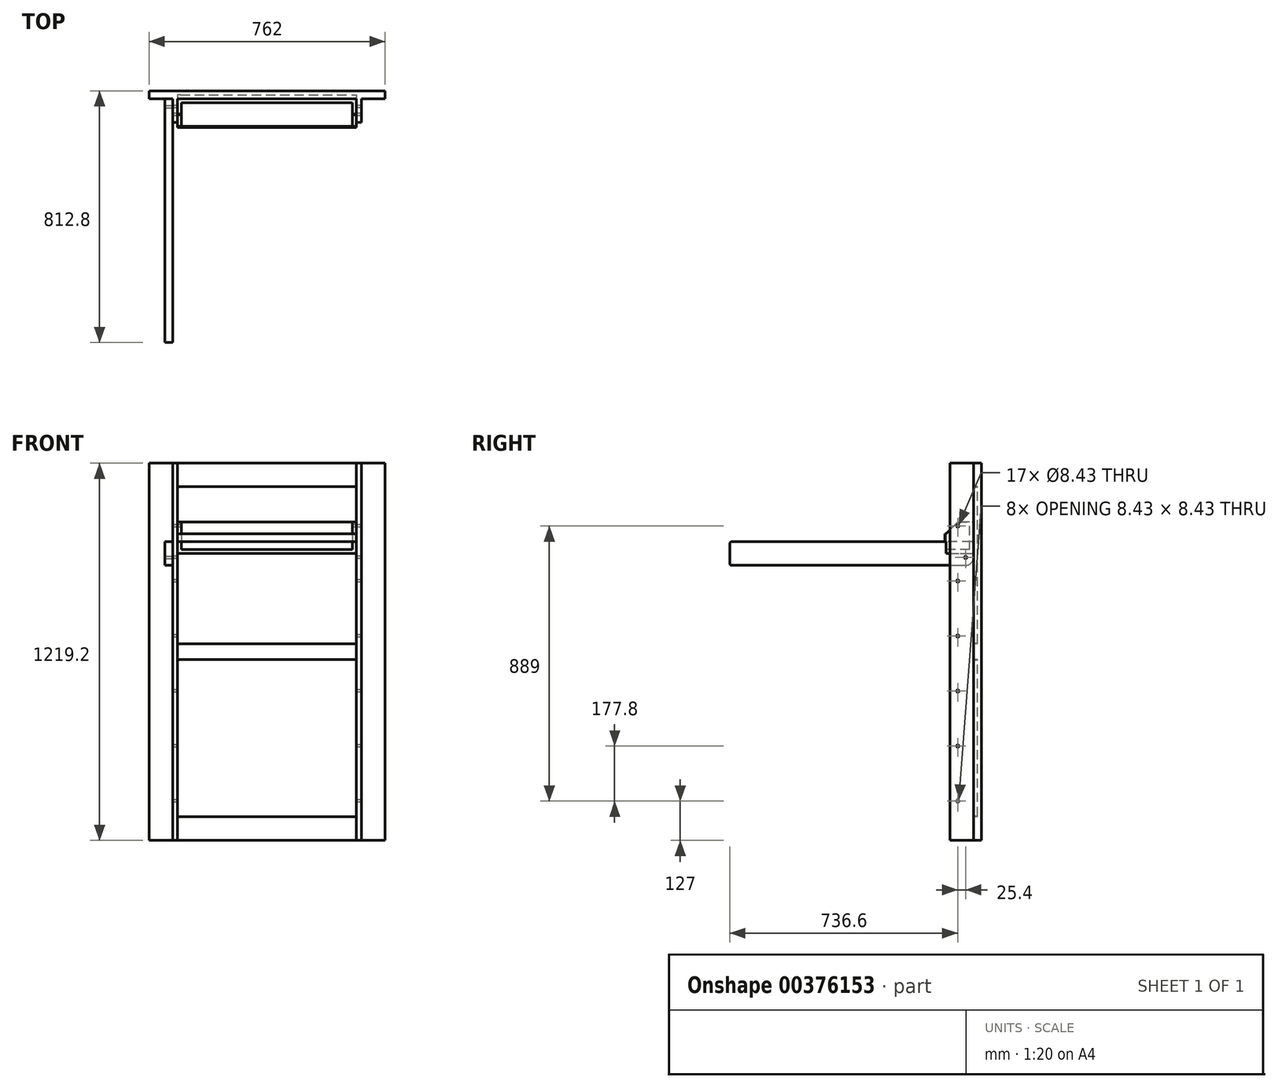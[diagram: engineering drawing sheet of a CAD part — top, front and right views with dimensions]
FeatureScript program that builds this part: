
annotation { "Feature Type Name" : "Feature", "Feature Type Description" : "" }
export const myFeature = defineFeature(function(context is Context, id is Id, definition is map)
    precondition{}
    {
        {
            var Q0;
            Q0=qCreatedBy(makeId("Front.planeOp"),FACE);
            var sketch = newSketch(context, id + "F0", { "sketchPlane" : qUnion([Q0])});
            skLineSegment(sketch, "E0.bottom", {"start": v(-381, 1219.2) * mm, "end": v(381, 1219.2) * mm});
            skLineSegment(sketch, "E0.top", {"start": v(-381, 0) * mm, "end": v(381, 0) * mm});
            skLineSegment(sketch, "E0.left", {"start": v(-381, 1219.2) * mm, "end": v(-381, 0) * mm});
            skLineSegment(sketch, "E0.right", {"start": v(381, 1219.2) * mm, "end": v(381, 0) * mm});
            skSolve(sketch);
        }
        {
            var Q0;
            Q0 = qSketchRegion(id + "F0", true);
            extrude(context, id + "F1", {"entities" : qUnion([Q0]), "depth" : 25.4 * mm});
        }
        {
            var Q0;
            Q0=makeQuery(id+"F1.opExtrude","CAP_FACE",FACE,{"disambiguationData":[OSD([sQuery(id+"F0.wireOp",EDGE,"E0.bottom"),sQuery(id+"F0.wireOp",EDGE,"E0.top"),sQuery(id+"F0.wireOp",EDGE,"E0.left"),sQuery(id+"F0.wireOp",EDGE,"E0.right")])],"isStart":false});
            var sketch = newSketch(context, id + "F2", { "sketchPlane" : qUnion([Q0])});
            skLineSegment(sketch, "E1.0", {"start": v(-279.4, 1143) * mm, "end": v(279.4, 1143) * mm});
            skLineSegment(sketch, "E1.1", {"start": v(-304.8, 1117.6) * mm, "end": v(-304.8, 660.4) * mm});
            skLineSegment(sketch, "E1.2", {"start": v(-279.4, 76.2) * mm, "end": v(279.4, 76.2) * mm});
            skLineSegment(sketch, "E1.3", {"start": v(304.8, 1117.6) * mm, "end": v(304.8, 660.4) * mm});
            skPoint(sketch, "E2.visualSharp", {"position": v(-304.8, 1143) * mm});
            skArc(sketch, "E2.filletArc", {"start": v(-279.4, 1143) * mm, "mid": v(-297.36, 1135.56) * mm, "end": v(-304.8, 1117.6) * mm});
            skPoint(sketch, "E3.visualSharp", {"position": v(304.8, 1143) * mm});
            skArc(sketch, "E3.filletArc", {"start": v(304.8, 1117.6) * mm, "mid": v(297.36, 1135.56) * mm, "end": v(279.4, 1143) * mm});
            skPoint(sketch, "E4.visualSharp", {"position": v(304.8, 76.2) * mm});
            skArc(sketch, "E4.filletArc", {"start": v(279.4, 76.2) * mm, "mid": v(297.36, 83.64) * mm, "end": v(304.8, 101.6) * mm});
            skPoint(sketch, "E5.visualSharp", {"position": v(-304.8, 76.2) * mm});
            skArc(sketch, "E5.filletArc", {"start": v(-304.8, 101.6) * mm, "mid": v(-297.36, 83.64) * mm, "end": v(-279.4, 76.2) * mm});
            skLineSegment(sketch, "E6.bottom", {"start": v(-279.4, 635) * mm, "end": v(279.4, 635) * mm});
            skLineSegment(sketch, "E6.top", {"start": v(-279.4, 584.2) * mm, "end": v(279.4, 584.2) * mm});
            skLineSegment(sketch, "E7.trimOffspring", {"start": v(-304.8, 558.8) * mm, "end": v(-304.8, 101.6) * mm});
            skLineSegment(sketch, "E8.trimOffspring", {"start": v(304.8, 558.8) * mm, "end": v(304.8, 101.6) * mm});
            skPoint(sketch, "E9.visualSharp", {"position": v(304.8, 635) * mm});
            skArc(sketch, "E9.filletArc", {"start": v(279.4, 635) * mm, "mid": v(297.36, 642.44) * mm, "end": v(304.8, 660.4) * mm});
            skPoint(sketch, "E10.visualSharp", {"position": v(-304.8, 635) * mm});
            skArc(sketch, "E10.filletArc", {"start": v(-304.8, 660.4) * mm, "mid": v(-297.36, 642.44) * mm, "end": v(-279.4, 635) * mm});
            skPoint(sketch, "E11.visualSharp", {"position": v(-304.8, 584.2) * mm});
            skArc(sketch, "E11.filletArc", {"start": v(-279.4, 584.2) * mm, "mid": v(-297.36, 576.76) * mm, "end": v(-304.8, 558.8) * mm});
            skPoint(sketch, "E12.visualSharp", {"position": v(304.8, 584.2) * mm});
            skArc(sketch, "E12.filletArc", {"start": v(304.8, 558.8) * mm, "mid": v(297.36, 576.76) * mm, "end": v(279.4, 584.2) * mm});
            skSolve(sketch);
        }
        {
            var Q0;
            Q0=makeQuery(id+"F2.imprint","IMPRINT",FACE,{"disambiguationData":[TD([[makeQuery(id+"F2.imprint","IMPRINT",EDGE,{"derivedFrom":sQuery(id+"F2.wireOp",EDGE,"E1.0")}),-1.0]])]});
            var Q1;
            Q1=makeQuery(id+"F2.imprint","IMPRINT",FACE,{"disambiguationData":[TD([[makeQuery(id+"F2.imprint","IMPRINT",EDGE,{"derivedFrom":sQuery(id+"F2.wireOp",EDGE,"E1.2")}),1.0]])]});
            extrude(context, id + "F3", {"entities" : qUnion([Q0, Q1]), "operationType" : NewBodyOperationType.REMOVE, "oppositeDirection" : true, "depth" : 12.7 * mm});
        }
        {
            var Q0;
            Q0=makeQuery(id+"F3.boolean.opBoolean","COPY",FACE,{"derivedFrom":makeQuery(id+"F3.opExtrude","CAP_FACE",FACE,{"disambiguationData":[OSD([sQuery(id+"F2.wireOp",EDGE,"E1.0"),sQuery(id+"F2.wireOp",EDGE,"E1.1"),sQuery(id+"F2.wireOp",EDGE,"E1.3"),sQuery(id+"F2.wireOp",EDGE,"E2.filletArc"),sQuery(id+"F2.wireOp",EDGE,"E3.filletArc"),sQuery(id+"F2.wireOp",EDGE,"E6.bottom"),sQuery(id+"F2.wireOp",EDGE,"E9.filletArc"),sQuery(id+"F2.wireOp",EDGE,"E10.filletArc")])],"isStart":false})});
            var sketch = newSketch(context, id + "F4", { "sketchPlane" : qUnion([Q0])});
            skLineSegment(sketch, "E13.0", {"start": v(-304.8, 1219.2) * mm, "end": v(-304.8, 0) * mm});
            skLineSegment(sketch, "E14", {"start": v(0, 0) * mm, "end": v(0, 1219.2) * mm, "construction": true});
            skLineSegment(sketch, "E15.MirrorCS", {"start": v(304.8, 1219.2) * mm, "end": v(304.8, 0) * mm});
            skLineSegment(sketch, "E16", {"start": v(-304.8, 1219.2) * mm, "end": v(-288.93, 1219.2) * mm});
            skLineSegment(sketch, "E17", {"start": v(-288.93, 1219.2) * mm, "end": v(-288.92, 0) * mm});
            skLineSegment(sketch, "E18", {"start": v(-288.92, 0) * mm, "end": v(-304.8, 0) * mm});
            skLineSegment(sketch, "E19", {"start": v(304.8, 0) * mm, "end": v(288.92, 0) * mm});
            skLineSegment(sketch, "E20", {"start": v(288.93, 0) * mm, "end": v(288.93, 1219.2) * mm});
            skLineSegment(sketch, "E21", {"start": v(288.93, 1219.2) * mm, "end": v(304.8, 1219.2) * mm});
            skSolve(sketch);
        }
        {
            var Q0;
            Q0 = qSketchRegion(id + "F4", true);
            extrude(context, id + "F5", {"entities" : qUnion([Q0]), "operationType" : NewBodyOperationType.ADD, "depth" : 88.9 * mm});
        }
        {
            var Q0;
            Q0=makeQuery(id+"F5.opExtrude","SWEPT_FACE",FACE,{"disambiguationData":[OSD([sQuery(id+"F4.wireOp",EDGE,"E13.0")])]});
            var sketch = newSketch(context, id + "F6", { "sketchPlane" : qUnion([Q0])});
            skLineSegment(sketch, "E22", {"start": v(76.2, 1219.2) * mm, "end": v(76.2, 0) * mm, "construction": true});
            skPoint(sketch, "E23", {"position": v(76.2, 1016) * mm});
            skPoint(sketch, "E24.0.1.0", {"position": v(76.2, 838.2) * mm});
            skPoint(sketch, "E24.0.2.0", {"position": v(76.2, 660.4) * mm});
            skPoint(sketch, "E24.0.3.0", {"position": v(76.2, 482.6) * mm});
            skPoint(sketch, "E24.0.4.0", {"position": v(76.2, 304.8) * mm});
            skPoint(sketch, "E24.0.5.0", {"position": v(76.2, 127) * mm});
            skLineSegment(sketch, "E24.direction1", {"start": v(76.2, 1016) * mm, "end": v(101.6, 1016) * mm, "construction": true});
            skLineSegment(sketch, "E24.direction2", {"start": v(76.2, 1016) * mm, "end": v(76.2, 838.2) * mm, "construction": true});
            skPoint(sketch, "E25", {"position": v(50.8, 914.4) * mm});
            skLineSegment(sketch, "E26", {"start": v(25.4, 914.4) * mm, "end": v(101.6, 914.4) * mm, "construction": true});
            skSolve(sketch);
        }
        {
            var Q0;
            Q0=sQuery(id+"F6.wireOp",VERTEX,"E23");
            var Q1;
            Q1=sQuery(id+"F6.wireOp",VERTEX,"E24.0.1.0");
            var Q2;
            Q2=sQuery(id+"F6.wireOp",VERTEX,"E24.0.2.0");
            var Q3;
            Q3=sQuery(id+"F6.wireOp",VERTEX,"E24.0.3.0");
            var Q4;
            Q4=sQuery(id+"F6.wireOp",VERTEX,"E24.0.4.0");
            var Q5;
            Q5=sQuery(id+"F6.wireOp",VERTEX,"E24.0.5.0");
            var Q6;
            Q6=sQuery(id+"F6.wireOp",VERTEX,"E25");
            var Q7;
            Q7=makeQuery(id+"F1.opExtrude","SWEPT_BODY",BODY,{"disambiguationData":[OSD([sQuery(id+"F0.wireOp",EDGE,"E0.bottom"),sQuery(id+"F0.wireOp",EDGE,"E0.top"),sQuery(id+"F0.wireOp",EDGE,"E0.left"),sQuery(id+"F0.wireOp",EDGE,"E0.right")])]});
            hole(context, id + "F7", {"style" : HoleStyle.SIMPLE, "endStyle" : HoleEndStyle.THROUGH, "standardTappedOrClearance" : lookupTablePath({ "standard" : "ANSI", "fit" : "Normal (ASME)", "size" : "5/16", "type" : "Clearance" }), "standardBlindInLast" : lookupTablePath({ "fit" : "Free", "standard" : "ANSI", "size" : "5/16", "type" : "Clearance" }), "holeDiameter" : 8.43 * mm, "isTappedThrough" : true, "tappedDepth" : 12.7 * mm, "tapClearance" : 3, "locations" : qUnion([Q0, Q1, Q2, Q3, Q4, Q5, Q6]), "scope" : qUnion([Q7])});
        }
        {
            var Q0;
            Q0=makeQuery(id+"F5.opExtrude","SWEPT_FACE",FACE,{"disambiguationData":[OSD([sQuery(id+"F4.wireOp",EDGE,"E17")])]});
            var sketch = newSketch(context, id + "F8", { "sketchPlane" : qUnion([Q0])});
            skCircle(sketch, "E27", {"center": v(-76.2, 1016) * mm, "radius": 4.22 * mm});
            skLineSegment(sketch, "E28.bottom", {"start": v(-76.2, 1028.7) * mm, "end": v(-25.4, 1028.7) * mm});
            skLineSegment(sketch, "E28.top", {"start": v(-114.3, 927.1) * mm, "end": v(-25.4, 927.1) * mm});
            skLineSegment(sketch, "E28.left", {"start": v(-114.3, 990.6) * mm, "end": v(-114.3, 927.1) * mm});
            skLineSegment(sketch, "E28.right", {"start": v(-25.4, 1028.7) * mm, "end": v(-25.4, 927.1) * mm});
            skLineSegment(sketch, "E29", {"start": v(-76.2, 1028.7) * mm, "end": v(-114.3, 990.6) * mm});
            skLineSegment(sketch, "E30", {"start": v(-76.2, 1028.7) * mm, "end": v(-114.3, 1028.7) * mm, "construction": true});
            skLineSegment(sketch, "E31", {"start": v(-114.3, 1028.7) * mm, "end": v(-114.3, 990.6) * mm, "construction": true});
            skSolve(sketch);
        }
        {
            var Q0;
            Q0 = qSketchRegion(id + "F8", true);
            extrude(context, id + "F9", {"entities" : qUnion([Q0]), "depth" : 577.85 * mm});
        }
        {
            var Q0;
            Q0=makeQuery(id+"F9.opExtrude","CAP_FACE",FACE,{"disambiguationData":[OSD([sQuery(id+"F8.wireOp",EDGE,"E27"),sQuery(id+"F8.wireOp",EDGE,"E28.bottom"),sQuery(id+"F8.wireOp",EDGE,"E28.top"),sQuery(id+"F8.wireOp",EDGE,"E28.left"),sQuery(id+"F8.wireOp",EDGE,"E28.right"),sQuery(id+"F8.wireOp",EDGE,"E29")])],"isStart":true});
            cPlane(context, id + "F10", {"entities" : qUnion([Q0]), "cplaneType" : CPlaneType.OFFSET, "offset" : 12.7 * mm, "oppositeDirection" : true, "width" : 152.4 * mm, "height" : 152.4 * mm});
        }
        {
            var Q0;
            Q0=qCreatedBy(id+"F10.planeOp",FACE);
            var sketch = newSketch(context, id + "F11", { "sketchPlane" : qUnion([Q0])});
            skLineSegment(sketch, "E32", {"start": v(114.3, 927.1) * mm, "end": v(114.3, 939.8) * mm, "construction": true});
            skLineSegment(sketch, "E33", {"start": v(38.1, 939.8) * mm, "end": v(114.3, 939.8) * mm});
            skLineSegment(sketch, "E34", {"start": v(38.1, 939.8) * mm, "end": v(38.1, 1028.7) * mm});
            skLineSegment(sketch, "E35", {"start": v(25.4, 1028.7) * mm, "end": v(38.1, 1028.7) * mm, "construction": true});
            skLineSegment(sketch, "E36", {"start": v(38.1, 1028.7) * mm, "end": v(114.3, 1028.7) * mm});
            skLineSegment(sketch, "E37", {"start": v(114.3, 1028.7) * mm, "end": v(114.3, 939.8) * mm});
            skSolve(sketch);
        }
        {
            var Q0;
            Q0 = qSketchRegion(id + "F11", true);
            extrude(context, id + "F12", {"entities" : qUnion([Q0]), "operationType" : NewBodyOperationType.REMOVE, "oppositeDirection" : true, "depth" : 552.45 * mm});
        }
        {
            var Q0;
            Q0=makeQuery(id+"F5.opExtrude","SWEPT_FACE",FACE,{"disambiguationData":[OSD([sQuery(id+"F4.wireOp",EDGE,"E13.0")])]});
            var sketch = newSketch(context, id + "F13", { "sketchPlane" : qUnion([Q0])});
            skCircle(sketch, "E38", {"center": v(50.8, 914.4) * mm, "radius": 4.22 * mm});
            skLineSegment(sketch, "E39", {"start": v(31.75, 965.2) * mm, "end": v(806.45, 965.2) * mm});
            skLineSegment(sketch, "E40", {"start": v(812.8, 958.85) * mm, "end": v(812.8, 895.35) * mm});
            skLineSegment(sketch, "E41", {"start": v(806.45, 889) * mm, "end": v(50.8, 889) * mm});
            skPoint(sketch, "E42.visualSharp", {"position": v(812.8, 965.2) * mm});
            skArc(sketch, "E42.filletArc", {"start": v(812.8, 958.85) * mm, "mid": v(810.94, 963.34) * mm, "end": v(806.45, 965.2) * mm});
            skPoint(sketch, "E43.visualSharp", {"position": v(812.8, 889) * mm});
            skArc(sketch, "E43.filletArc", {"start": v(806.45, 889) * mm, "mid": v(810.94, 890.86) * mm, "end": v(812.8, 895.35) * mm});
            skLineSegment(sketch, "E44", {"start": v(50.8, 914.4) * mm, "end": v(812.8, 914.4) * mm, "construction": true});
            skLineSegment(sketch, "E45", {"start": v(25.4, 914.4) * mm, "end": v(25.4, 958.85) * mm});
            skArc(sketch, "E46", {"start": v(25.4, 914.4) * mm, "mid": v(32.84, 896.44) * mm, "end": v(50.8, 889) * mm});
            skPoint(sketch, "E47.visualSharp", {"position": v(25.4, 965.2) * mm});
            skArc(sketch, "E47.filletArc", {"start": v(31.75, 965.2) * mm, "mid": v(27.26, 963.34) * mm, "end": v(25.4, 958.85) * mm});
            skSolve(sketch);
        }
        {
            var Q0;
            Q0 = qSketchRegion(id + "F13", true);
            extrude(context, id + "F14", {"entities" : qUnion([Q0]), "depth" : 25.4 * mm});
        }
        {
            var Q0;
            Q0=makeQuery(id+"F9.opExtrude","SWEPT_FACE",FACE,{"disambiguationData":[OSD([sQuery(id+"F8.wireOp",EDGE,"E28.left")])]});
            var sketch = newSketch(context, id + "F15", { "sketchPlane" : qUnion([Q0])});
            skLineSegment(sketch, "E48.bottom", {"start": v(-288.93, 990.6) * mm, "end": v(288.92, 990.6) * mm});
            skLineSegment(sketch, "E48.top", {"start": v(-288.93, 965.2) * mm, "end": v(288.92, 965.2) * mm});
            skLineSegment(sketch, "E48.left", {"start": v(-288.93, 990.6) * mm, "end": v(-288.93, 965.2) * mm});
            skLineSegment(sketch, "E48.right", {"start": v(288.92, 990.6) * mm, "end": v(288.92, 965.2) * mm});
            skSolve(sketch);
        }
        {
            var Q0;
            Q0 = qSketchRegion(id + "F15", true);
            extrude(context, id + "F16", {"entities" : qUnion([Q0]), "operationType" : NewBodyOperationType.ADD, "depth" : 3.17 * mm});
        }
    });
